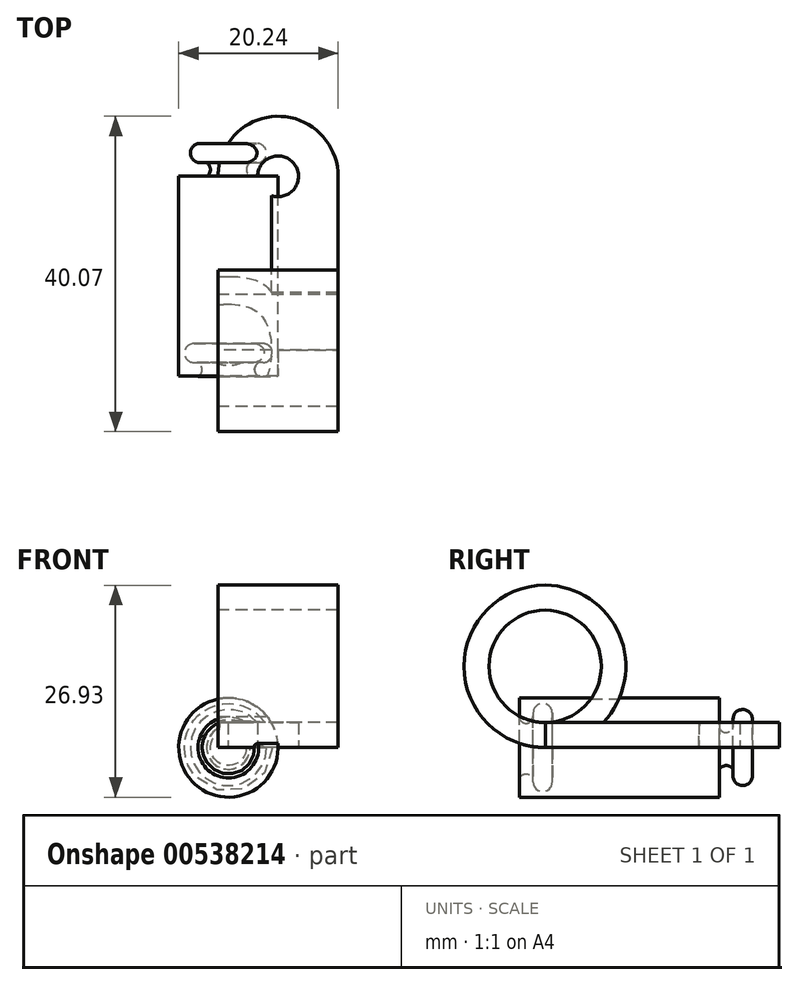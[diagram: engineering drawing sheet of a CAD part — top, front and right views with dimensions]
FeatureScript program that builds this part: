
annotation { "Feature Type Name" : "Feature", "Feature Type Description" : "" }
export const myFeature = defineFeature(function(context is Context, id is Id, definition is map)
    precondition{}
    {
        {
            var Q0;
            Q0=qCreatedBy(makeId("Top.planeOp"),FACE);
            var sketch = newSketch(context, id + "F0", { "sketchPlane" : qUnion([Q0])});
            skLineSegment(sketch, "E0", {"start": v(0, 0) * mm, "end": v(0, -25.4) * mm});
            skLineSegment(sketch, "E1", {"start": v(0, 0) * mm, "end": v(-3.55, 0) * mm});
            skArc(sketch, "E2", {"start": v(-3.55, 1.71) * mm, "mid": v(-4.02, 0.86) * mm, "end": v(-3.55, 0) * mm});
            skLineSegment(sketch, "E3", {"start": v(-3.55, 1.71) * mm, "end": v(-2.7, 1.71) * mm});
            skArc(sketch, "E4", {"start": v(-2.7, 1.71) * mm, "mid": v(-1.47, 2.95) * mm, "end": v(-2.7, 4.18) * mm});
            skLineSegment(sketch, "E5", {"start": v(-6.3, 4.16) * mm, "end": v(-2.7, 4.18) * mm});
            skArc(sketch, "E6", {"start": v(-2.46, -23.66) * mm, "mid": v(-2.97, -24.54) * mm, "end": v(-2.46, -25.42) * mm});
            skLineSegment(sketch, "E7", {"start": v(-2.46, -23.66) * mm, "end": v(-1.92, -23.66) * mm});
            skArc(sketch, "E8", {"start": v(-1.92, -23.66) * mm, "mid": v(-0.71, -22.46) * mm, "end": v(-1.92, -21.25) * mm});
            skLineSegment(sketch, "E9", {"start": v(-2.46, -25.42) * mm, "end": v(0, -25.4) * mm});
            skLineSegment(sketch, "E10", {"start": v(-6.3, 4.16) * mm, "end": v(-6.3, -21.28) * mm});
            skLineSegment(sketch, "E11", {"start": v(-6.3, -21.28) * mm, "end": v(-1.92, -21.25) * mm});
            skSolve(sketch);
        }
        {
            var Q0;
            Q0 = qSketchRegion(id + "F0", true);
            var Q1;
            Q1=sQuery(id+"F0.wireOp",EDGE,"E10");
            revolve(context, id + "F1", {"entities" : qUnion([Q0]), "axis" : qUnion([Q1]), "revolveType" : RevolveType.FULL});
        }
        {
            var Q0;
            Q0=qCreatedBy(makeId("Top.planeOp"),FACE);
            var sketch = newSketch(context, id + "F2", { "sketchPlane" : qUnion([Q0])});
            skCircle(sketch, "E12", {"center": v(0, 0) * mm, "radius": 2.6 * mm});
            skPoint(sketch, "E13", {"position": v(-7.62, 0) * mm});
            skPoint(sketch, "E14", {"position": v(7.62, 0) * mm});
            skLineSegment(sketch, "E15", {"start": v(-7.62, 0) * mm, "end": v(-7.62, 0) * mm});
            skLineSegment(sketch, "E16", {"start": v(7.62, 0) * mm, "end": v(7.62, -22.1) * mm});
            skLineSegment(sketch, "E17", {"start": v(-7.62, 0) * mm, "end": v(-7.62, -22.1) * mm});
            skArc(sketch, "E18", {"start": v(7.62, 0) * mm, "mid": v(0, 7.62) * mm, "end": v(-7.62, 0) * mm});
            skLineSegment(sketch, "E19", {"start": v(-7.62, -22.1) * mm, "end": v(7.62, -22.1) * mm});
            skPoint(sketch, "E20", {"position": v(7.41, -22.1) * mm});
            skSolve(sketch);
        }
        {
            var Q0;
            Q0=qCreatedBy(makeId("Right.planeOp"),FACE);
            var sketch = newSketch(context, id + "F3", { "sketchPlane" : qUnion([Q0])});
            skLineSegment(sketch, "E21", {"start": v(-393.97, 0) * mm, "end": v(-393.97, 20.62) * mm});
            skLineSegment(sketch, "E22", {"start": v(-22.13, 0) * mm, "end": v(-22.13, 20.62) * mm, "construction": true});
            skArc(sketch, "E23", {"start": v(-22.13, 20.62) * mm, "mid": v(-32.45, 10.31) * mm, "end": v(-22.13, 0) * mm});
            skPoint(sketch, "E24", {"position": v(-22.13, 3.18) * mm});
            skPoint(sketch, "E25", {"position": v(-22.13, 17.45) * mm});
            skArc(sketch, "E26", {"start": v(-22.13, 17.45) * mm, "mid": v(-29.27, 10.31) * mm, "end": v(-22.13, 3.18) * mm});
            skPoint(sketch, "E27", {"position": v(-29.27, 10.31) * mm});
            skPoint(sketch, "E28", {"position": v(-32.45, 10.31) * mm});
            skLineSegment(sketch, "E29", {"start": v(-22.13, 17.45) * mm, "end": v(-22.13, 20.62) * mm});
            skLineSegment(sketch, "E30", {"start": v(-22.13, 0) * mm, "end": v(-22.13, 3.18) * mm});
            skArc(sketch, "E31", {"start": v(-22.13, 3.18) * mm, "mid": v(-15.01, 10.31) * mm, "end": v(-22.13, 17.45) * mm});
            skArc(sketch, "E32", {"start": v(-22.13, 0) * mm, "mid": v(-11.9, 10.31) * mm, "end": v(-22.13, 20.62) * mm});
            skLineSegment(sketch, "E33", {"start": v(-22.13, 3.17) * mm, "end": v(-12.5, 3.2) * mm, "construction": true});
            skSolve(sketch);
        }
        {
            var Q0;
            Q0 = qSketchRegion(id + "F2", true);
            extrude(context, id + "F4", {"entities" : qUnion([Q0]), "depth" : 3.17 * mm, "offsetDistance" : 25.4 * mm});
        }
        {
            var Q0;
            Q0 = qSketchRegion(id + "F3", true);
            extrude(context, id + "F5", {"entities" : qUnion([Q0]), "depth" : 7.6 * mm, "offsetDistance" : 25.4 * mm});
        }
        {
            var Q0;
            Q0=makeQuery(id+"F5.opExtrude","CAP_FACE",FACE,{"disambiguationData":[OSD([sQuery(id+"F3.wireOp",EDGE,"E23"),sQuery(id+"F3.wireOp",EDGE,"E26"),sQuery(id+"F3.wireOp",EDGE,"E29"),sQuery(id+"F3.wireOp",EDGE,"E30")])],"isStart":true});
            var Q1;
            Q1 = qSketchRegion(id + "F3", true);
            extrude(context, id + "F6", {"entities" : qUnion([Q0, Q1]), "operationType" : NewBodyOperationType.ADD, "depth" : 7.62 * mm, "offsetDistance" : 25.4 * mm});
        }
    });
